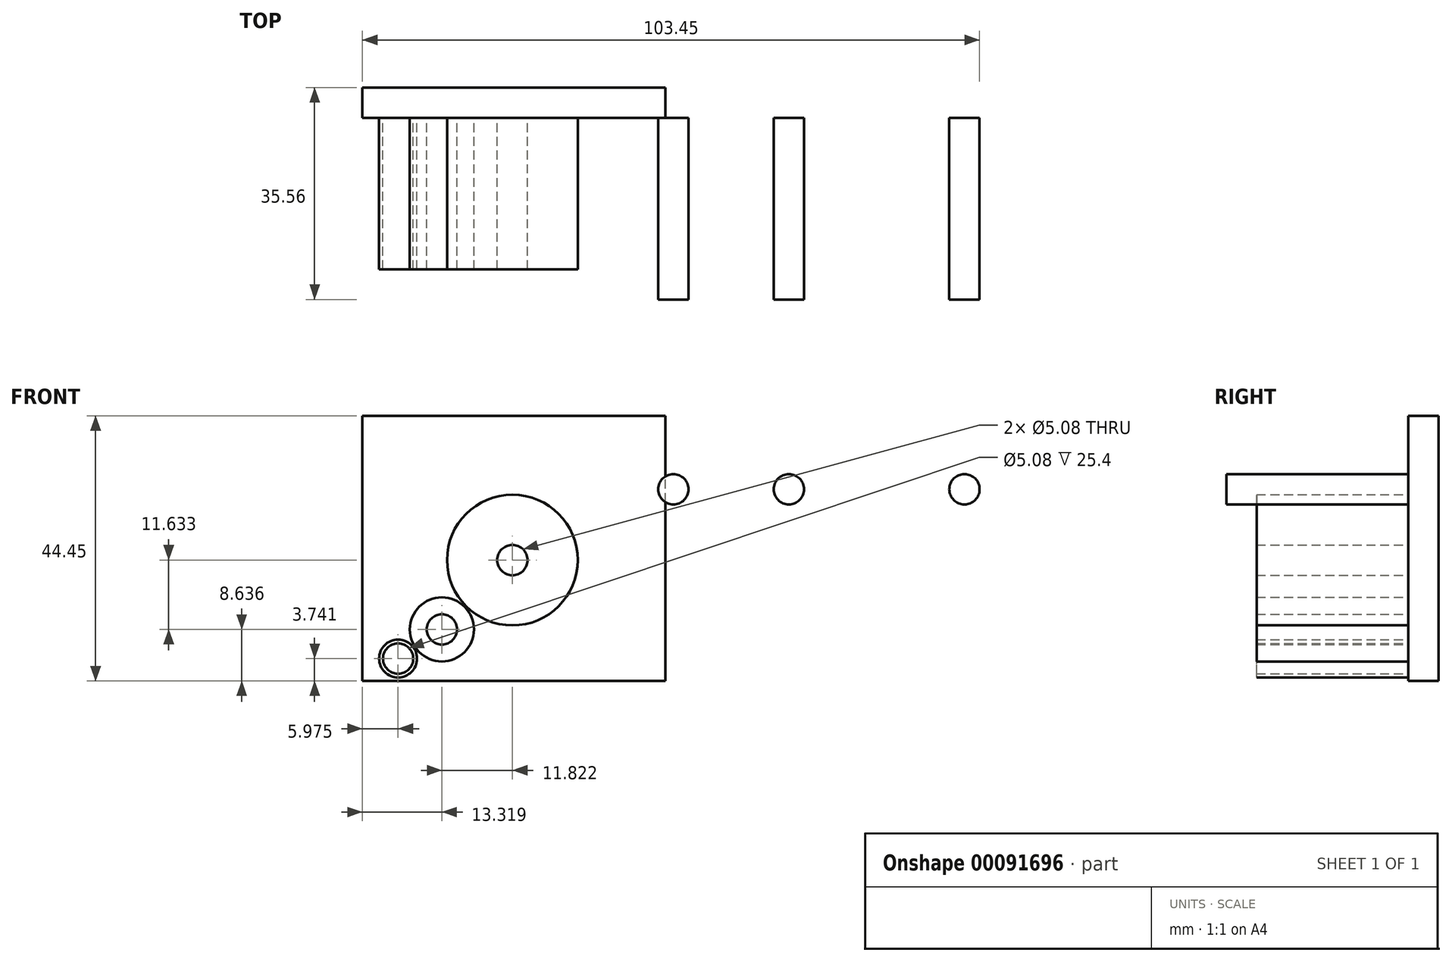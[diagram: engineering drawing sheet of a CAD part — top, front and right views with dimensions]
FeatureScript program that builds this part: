
annotation { "Feature Type Name" : "Feature", "Feature Type Description" : "" }
export const myFeature = defineFeature(function(context is Context, id is Id, definition is map)
    precondition{}
    {
        {
            var Q0;
            Q0=qCreatedBy(makeId("Front.planeOp"),FACE);
            var sketch = newSketch(context, id + "F0", { "sketchPlane" : qUnion([Q0])});
            skLineSegment(sketch, "E0.bottom", {"start": v(-43.77, -32.14) * mm, "end": v(7.03, -32.14) * mm});
            skLineSegment(sketch, "E0.top", {"start": v(-43.77, 12.31) * mm, "end": v(7.03, 12.31) * mm});
            skLineSegment(sketch, "E0.left", {"start": v(-43.77, -32.14) * mm, "end": v(-43.77, 12.31) * mm});
            skLineSegment(sketch, "E0.right", {"start": v(7.03, -32.14) * mm, "end": v(7.03, 12.31) * mm});
            skSolve(sketch);
        }
        {
            var Q0;
            Q0=qCreatedBy(makeId("Front.planeOp"),FACE);
            var sketch = newSketch(context, id + "F1", { "sketchPlane" : qUnion([Q0])});
            skCircle(sketch, "E1", {"center": v(-18.63, -11.87) * mm, "radius": 10.96 * mm});
            skCircle(sketch, "E2", {"center": v(-30.45, -23.5) * mm, "radius": 5.37 * mm});
            skCircle(sketch, "E3", {"center": v(-37.8, -28.4) * mm, "radius": 3.18 * mm});
            skCircle(sketch, "E4", {"center": v(-18.63, -11.87) * mm, "radius": 2.54 * mm});
            skCircle(sketch, "E5", {"center": v(-30.45, -23.5) * mm, "radius": 2.54 * mm});
            skCircle(sketch, "E6", {"center": v(-37.8, -28.4) * mm, "radius": 2.54 * mm});
            skSolve(sketch);
        }
        {
            var Q0;
            Q0=makeQuery(id+"F1.imprint","IMPRINT",FACE,{"disambiguationData":[TD([[makeQuery(id+"F1.imprint","IMPRINT",EDGE,{"derivedFrom":sQuery(id+"F1.wireOp",EDGE,"E1")}),1.0]])]});
            extrude(context, id + "F2", {"entities" : qUnion([Q0]), "depth" : 25.4 * mm});
        }
        {
            var Q0;
            Q0=makeQuery(id+"F1.imprint","IMPRINT",FACE,{"disambiguationData":[TD([[makeQuery(id+"F1.imprint","IMPRINT",EDGE,{"derivedFrom":sQuery(id+"F1.wireOp",EDGE,"E2")}),1.0]])]});
            extrude(context, id + "F3", {"entities" : qUnion([Q0]), "depth" : 25.4 * mm});
        }
        {
            var Q0;
            Q0=makeQuery(id+"F1.imprint","IMPRINT",FACE,{"disambiguationData":[TD([[makeQuery(id+"F1.imprint","IMPRINT",EDGE,{"derivedFrom":sQuery(id+"F1.wireOp",EDGE,"E3")}),1.0]])]});
            extrude(context, id + "F4", {"entities" : qUnion([Q0]), "depth" : 25.4 * mm});
        }
        {
            var Q0;
            Q0=makeQuery(id+"F0.imprint","IMPRINT",FACE,{"disambiguationData":[TD([[makeQuery(id+"F0.imprint","IMPRINT",EDGE,{"derivedFrom":sQuery(id+"F0.wireOp",EDGE,"E0.bottom")}),1.0]])]});
            extrude(context, id + "F5", {"entities" : qUnion([Q0]), "oppositeDirection" : true, "depth" : 5.08 * mm});
        }
        {
            var Q0;
            Q0=qCreatedBy(makeId("Front.planeOp"),FACE);
            var sketch = newSketch(context, id + "F6", { "sketchPlane" : qUnion([Q0])});
            skCircle(sketch, "E7", {"center": v(8.35, 0) * mm, "radius": 2.54 * mm});
            skCircle(sketch, "E8", {"center": v(27.7, 0) * mm, "radius": 2.54 * mm});
            skCircle(sketch, "E9", {"center": v(57.14, 0) * mm, "radius": 2.54 * mm});
            skSolve(sketch);
        }
        {
            var Q0;
            Q0=makeQuery(id+"F6.imprint","IMPRINT",FACE,{"disambiguationData":[TD([[makeQuery(id+"F6.imprint","IMPRINT",EDGE,{"derivedFrom":sQuery(id+"F6.wireOp",EDGE,"E7")}),1.0]])]});
            extrude(context, id + "F7", {"entities" : qUnion([Q0]), "depth" : 30.48 * mm});
        }
        {
            var Q0;
            Q0=makeQuery(id+"F6.imprint","IMPRINT",FACE,{"disambiguationData":[TD([[makeQuery(id+"F6.imprint","IMPRINT",EDGE,{"derivedFrom":sQuery(id+"F6.wireOp",EDGE,"E8")}),1.0]])]});
            extrude(context, id + "F8", {"entities" : qUnion([Q0]), "depth" : 30.48 * mm});
        }
        {
            var Q0;
            Q0=makeQuery(id+"F6.imprint","IMPRINT",FACE,{"disambiguationData":[TD([[makeQuery(id+"F6.imprint","IMPRINT",EDGE,{"derivedFrom":sQuery(id+"F6.wireOp",EDGE,"E9")}),1.0]])]});
            extrude(context, id + "F9", {"entities" : qUnion([Q0]), "depth" : 30.48 * mm});
        }
    });
